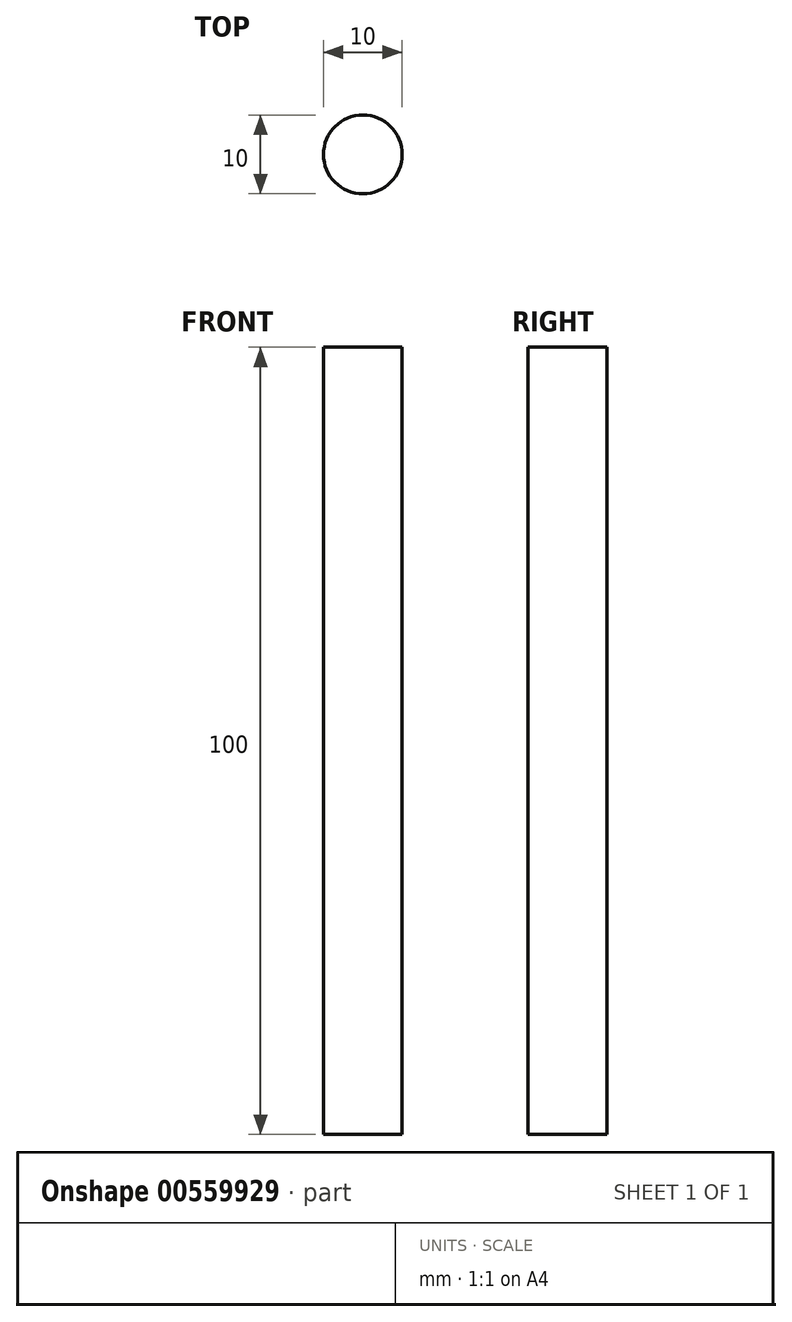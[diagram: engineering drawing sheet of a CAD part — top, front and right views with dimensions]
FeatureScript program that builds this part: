
annotation { "Feature Type Name" : "Feature", "Feature Type Description" : "" }
export const myFeature = defineFeature(function(context is Context, id is Id, definition is map)
    precondition{}
    {
        {
            var Q0;
            Q0=qCreatedBy(makeId("Top.planeOp"),FACE);
            var sketch = newSketch(context, id + "F0", { "sketchPlane" : qUnion([Q0])});
            skCircle(sketch, "E0", {"center": v(10, 0) * mm, "radius": 5 * mm});
            skSolve(sketch);
        }
        {
            var Q0;
            Q0 = qSketchRegion(id + "F0", true);
            extrude(context, id + "F1", {"entities" : qUnion([Q0]), "depth" : 100 * mm, "offsetDistance" : 25 * mm});
        }
    });
